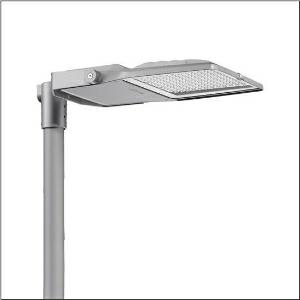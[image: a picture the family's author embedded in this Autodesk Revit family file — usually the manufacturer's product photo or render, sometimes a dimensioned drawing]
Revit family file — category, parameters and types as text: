
# Revit family: floodlight_fl_21_iq_midi___pl33t_5xa7781f2f3a_a5b2
name_source: partatom
category: Lighting Fixtures
units: mm (PartAtom-declared; Revit-internal decimal feet)

## family parameters
Cut with Voids When Loaded = No
Host = Face
Light Source = No
Part Type = Normal
Room Calculation Point = No
Round Connector Dimension = Use Diameter
Shared = No

## types (1)
- --- (1 x LED, 35350 lm, 270.2 W, 3000K)
    Apparent Load = 270 VA
    CIE Flux Codes = 26 75 99 100 100
    Color Rendering = 70
    Color Temperature = 3000K
    Default Elevation = 1800 mm
    Description = Floodlight FL 21 iQ midi, floodlight, primary light control with lens, of PMMA, primary optical cover: protective disc, of toughened safety glass, transparent, light distribution: PL33T, light emission: direct distribution, installation type: surface-mounted, LED, High Power LED, rated luminous flux: 35.350lm, luminous efficacy: 131lm/W, light colour: 730, colour temperature: 3000K, control gear: iQ Comfort/DALI, control: optimised constant luminous flux control (CLO 2.0), Desk-Remote (wireless, voltage-free reading and setting of iQ features in the workshop via application-optimized NFC function/RFID function), Light-Fading, Smart-Wire, Night-Set, Lumen-Switch, Temp-Guard, Auto-Match, with terminal, 6-pole, mains connection: 220..240V, AC, 50/60Hz, start of lifetime: 270W, end of service life: 287W, reduction: 117W, luminaire housing, of diecast aluminium, powder-coated, Siteco® metallic grey (DB 702S), corrosivity category C5 mid according to DIN EN ISO 12944, suitable for swimming pools, chlorine-resistant, sealing non-destructively replaceable, please order mast flange separately, mast bracket, of steel, galvanised, powder-coated, Siteco® metallic grey (DB 702S), protection rating (complete): IP66, insulation class (complete): insulation class II (safety insulation), certification: CE, ENEC, VDE, protection symbol: D, impact resistance: IK08, permissible operating ambient temperature: -40..+40°C, permissible operating ambient temperature for outdoor applications: -40..+50°C, standard: DIN EN 12944, LABS conformity tested according to VDMA 24364:2018-05, packaging unit: 1 piece

Light Distribution: PL33T
    Height = 76 mm
    Lamp = 1 x LED
    Lamp Light Flux = 35350 lm
    Lamp Power = 270.2 W
    Lamp count = 1
    Length = 657 mm
    Luminous efficacy = 131 lm/W
    Manufacturer = Siteco
    ModVariant = No
    Model = 5XA7781F2F3A
    Number of Poles = 1
    OnlyDefault = Yes
    Power Factor = 1
    Product Name = Floodlight FL 21 iQ midi | PL33T
    Product group = floodlight | pylon annexe
    ProductGroupID = 6200
    Protection Class = Protection class II
    Protection Degree = IP 66
    RLX_Detail_Level = 1
    RLX_Emergency_Light_Flux = 0 lm
    RLX_Emergency_Type = 0
    RLX_Emergency_Type_DB = No
    RlxData = <blob elided: 153549 chars, md5=131eafd6>
    Socket = socket
    Standby Power = 0 W
    System Light Flux = 35350 lm
    System Power = 270 W
    Type Comments = factory setting: luminous flux: 100 % | dim-lin: 254 | 620 mA
    Type Image = l_1007123.jpg
    URL = http://relux.com
    VarID = @adj_103564
    Voltage = 0 V
    Weight = 0.00 kg
    Width = 442 mm

## geometry (parser evidence)
native form markers: Blend x4, Sweep x14
no freeform markers — native parametric forms only
